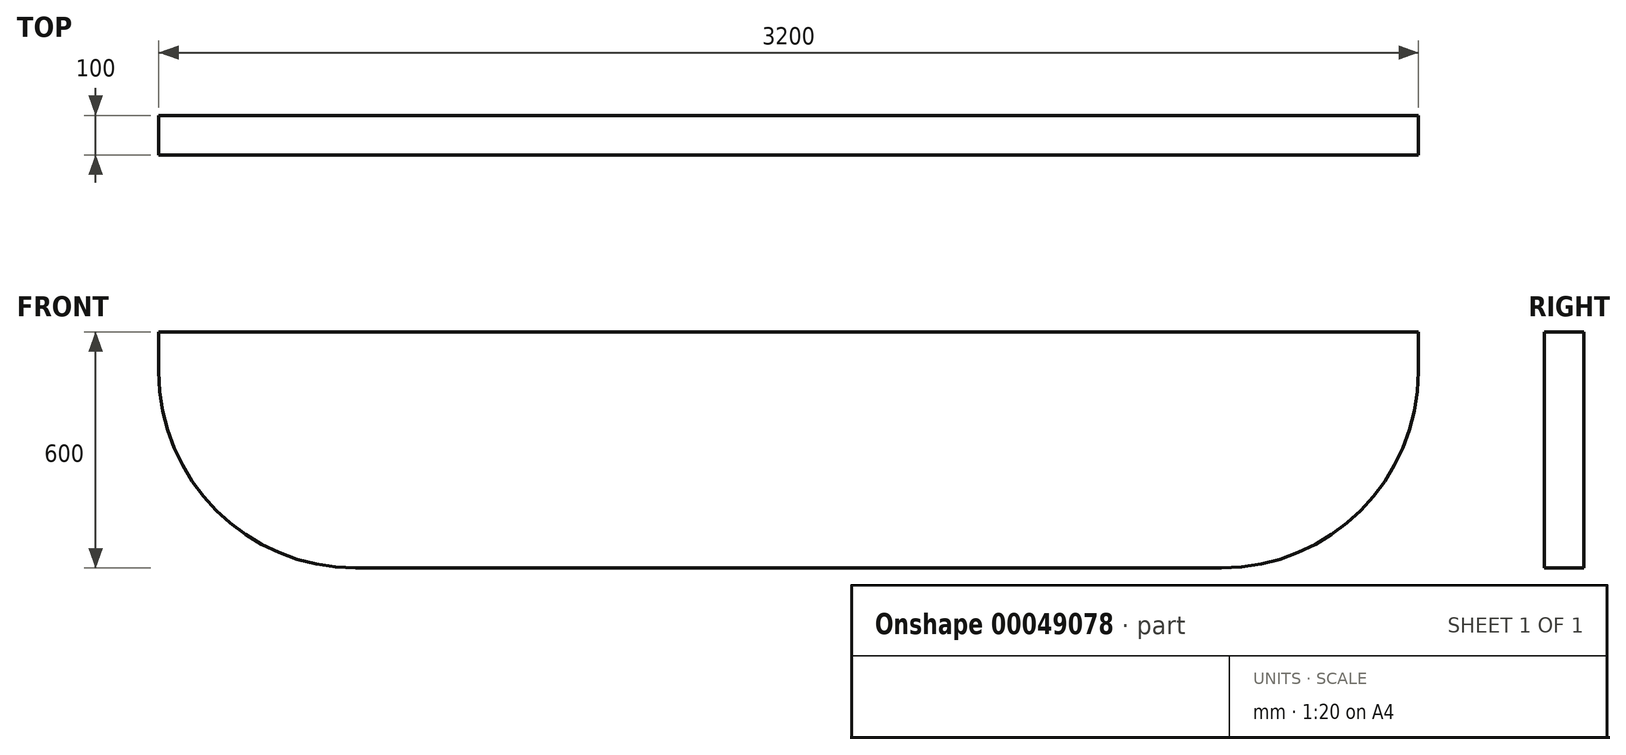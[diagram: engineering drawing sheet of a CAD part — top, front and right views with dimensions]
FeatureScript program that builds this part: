
annotation { "Feature Type Name" : "Feature", "Feature Type Description" : "" }
export const myFeature = defineFeature(function(context is Context, id is Id, definition is map)
    precondition{}
    {
        {
            var Q0;
            Q0=qCreatedBy(makeId("Front.planeOp"),FACE);
            var sketch = newSketch(context, id + "F0", { "sketchPlane" : qUnion([Q0])});
            skLineSegment(sketch, "E0.bottom", {"start": v(0, 0) * mm, "end": v(3200, 0) * mm});
            skLineSegment(sketch, "E0.top", {"start": v(0, -600) * mm, "end": v(3200, -600) * mm});
            skLineSegment(sketch, "E0.left", {"start": v(0, 0) * mm, "end": v(0, -600) * mm});
            skLineSegment(sketch, "E0.right", {"start": v(3200, 0) * mm, "end": v(3200, -600) * mm});
            skSolve(sketch);
        }
        {
            var Q0;
            Q0=makeQuery(id+"F0.imprint","IMPRINT",FACE,{"disambiguationData":[TD([[makeQuery(id+"F0.imprint","IMPRINT",EDGE,{"derivedFrom":sQuery(id+"F0.wireOp",EDGE,"E0.bottom")}),-1.0]])]});
            extrude(context, id + "F1", {"entities" : qUnion([Q0]), "depth" : 100 * mm});
        }
        {
            var Q0;
            Q0=makeQuery(id+"F1.opExtrude","SWEPT_EDGE",EDGE,{"disambiguationData":[OSD([sQuery(id+"F0.wireOp",EDGE,"E0.top"),sQuery(id+"F0.wireOp",EDGE,"E0.right")])]});
            var Q1;
            Q1=makeQuery(id+"F1.opExtrude","SWEPT_EDGE",EDGE,{"disambiguationData":[OSD([sQuery(id+"F0.wireOp",EDGE,"E0.top"),sQuery(id+"F0.wireOp",EDGE,"E0.left")])]});
            fillet(context, id + "F2", {"entities" : qUnion([Q0, Q1]), "radius" : 500 * mm, "tangentPropagation" : true, "allowEdgeOverflow" : false});
        }
    });
